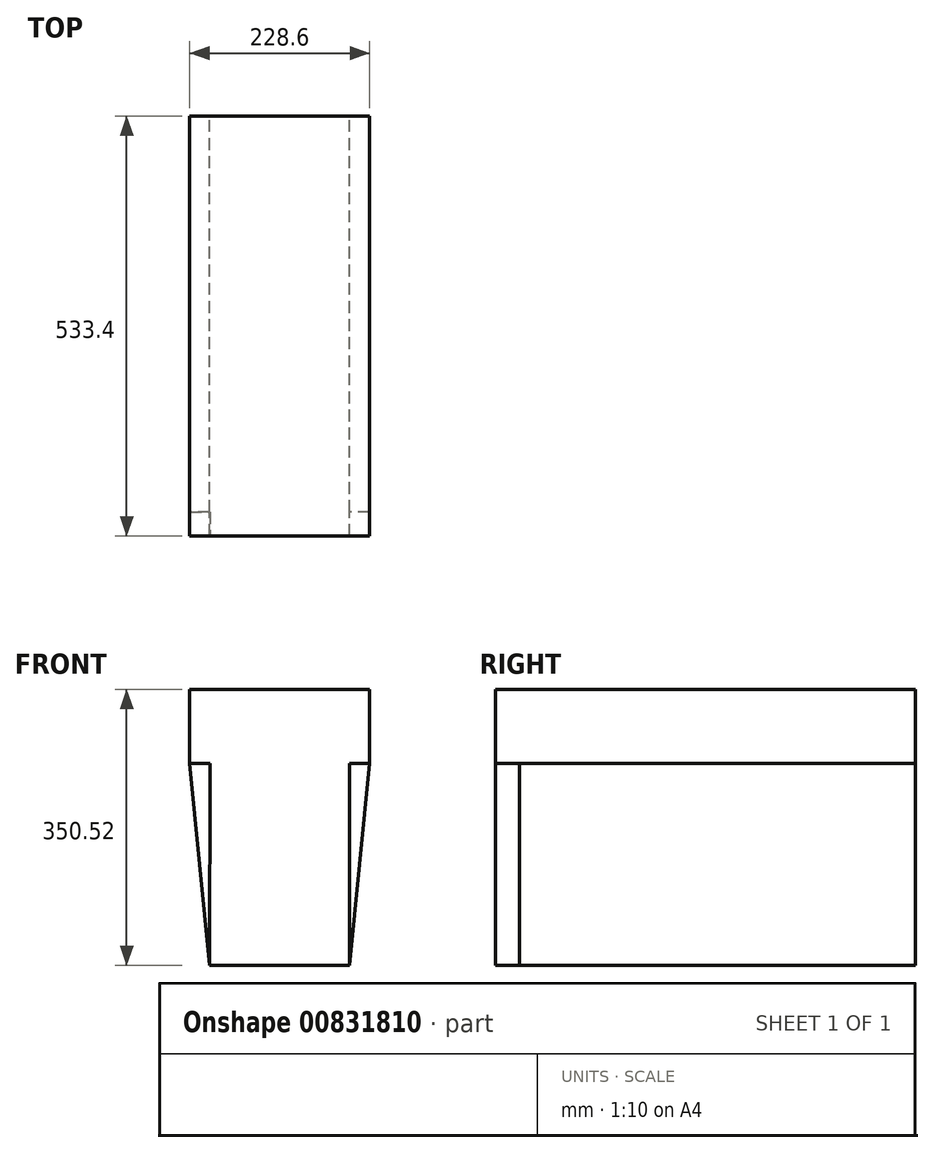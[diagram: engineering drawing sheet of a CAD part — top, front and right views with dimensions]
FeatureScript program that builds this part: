
annotation { "Feature Type Name" : "Feature", "Feature Type Description" : "" }
export const myFeature = defineFeature(function(context is Context, id is Id, definition is map)
    precondition{}
    {
        {
            var Q0;
            Q0=qCreatedBy(makeId("Front.planeOp"),FACE);
            var sketch = newSketch(context, id + "F0", { "sketchPlane" : qUnion([Q0])});
            skLineSegment(sketch, "E0", {"start": v(-248.62, 194.68) * mm, "end": v(-20.02, 194.68) * mm});
            skLineSegment(sketch, "E1", {"start": v(-20.02, 194.68) * mm, "end": v(-20.02, 100.7) * mm});
            skLineSegment(sketch, "E2", {"start": v(-20.02, 100.7) * mm, "end": v(-45.42, -155.84) * mm});
            skLineSegment(sketch, "E3", {"start": v(-45.42, -155.84) * mm, "end": v(-223.22, -155.84) * mm});
            skLineSegment(sketch, "E4", {"start": v(-223.22, -155.84) * mm, "end": v(-248.62, 100.7) * mm});
            skLineSegment(sketch, "E5", {"start": v(-248.62, 100.7) * mm, "end": v(-248.62, 194.68) * mm});
            skLineSegment(sketch, "E6", {"start": v(-248.62, 100.7) * mm, "end": v(-223.22, 100.7) * mm});
            skLineSegment(sketch, "E7", {"start": v(-223.22, 100.7) * mm, "end": v(-224.78, -140.09) * mm});
            skLineSegment(sketch, "E8", {"start": v(-20.02, 100.7) * mm, "end": v(-45.42, 100.7) * mm});
            skLineSegment(sketch, "E9", {"start": v(-45.42, 100.7) * mm, "end": v(-43.86, -140.09) * mm});
            skSolve(sketch);
        }
        {
            var Q0;
            Q0=qSketchRegion(id+"F0",true);
            extrude(context, id + "F1", {"entities" : qUnion([Q0]), "depth" : 533.4 * mm, "offsetDistance" : 25.4 * mm});
        }
        {
            var Q0;
            Q0=makeQuery(id+"F1.opExtrude","CAP_FACE",FACE,{"disambiguationData":[OSD([sQuery(id+"F0.wireOp",EDGE,"E0"),sQuery(id+"F0.wireOp",EDGE,"E1"),sQuery(id+"F0.wireOp",EDGE,"E2"),sQuery(id+"F0.wireOp",EDGE,"E3"),sQuery(id+"F0.wireOp",EDGE,"E4"),sQuery(id+"F0.wireOp",EDGE,"E5")])],"isStart":false});
            var sketch = newSketch(context, id + "F2", { "sketchPlane" : qUnion([Q0])});
            skLineSegment(sketch, "E10", {"start": v(-248.62, 100.7) * mm, "end": v(-223.08, 100.7) * mm});
            skLineSegment(sketch, "E11", {"start": v(-223.22, -155.84) * mm, "end": v(-248.62, 100.7) * mm});
            skLineSegment(sketch, "E12", {"start": v(-15.6, 100.7) * mm, "end": v(-45.42, 100.7) * mm});
            skLineSegment(sketch, "E13", {"start": v(-45.42, 100.7) * mm, "end": v(-45.42, -155.84) * mm});
            skLineSegment(sketch, "E14", {"start": v(-45.42, -155.84) * mm, "end": v(-20.02, 100.7) * mm});
            skLineSegment(sketch, "E15", {"start": v(-223.22, -155.84) * mm, "end": v(-223.08, 100.7) * mm});
            skSolve(sketch);
        }
        {
            var Q0;
            Q0=makeQuery(id+"F2.imprint","IMPRINT",FACE,{"disambiguationData":[TD([[makeQuery(id+"F2.imprint","IMPRINT",EDGE,{"derivedFrom":sQuery(id+"F2.wireOp",EDGE,"E10")}),-1.0]])]});
            var Q1;
            {var subQ2=sQuery(id+"F2.wireOp",EDGE,"E13");Q1=makeQuery(id+"F2.imprint","IMPRINT",FACE,{"disambiguationData":[TD([[makeQuery(id+"F2.imprint","IMPRINT",EDGE,{"derivedFrom":subQ2}),1.0]])]});}
            extrude(context, id + "F3", {"entities" : qUnion([Q0, Q1]), "operationType" : NewBodyOperationType.REMOVE, "oppositeDirection" : true, "depth" : 30.48 * mm, "offsetDistance" : 25.4 * mm});
        }
        {
            var Q0;
            Q0=makeQuery(id+"F0.imprint","IMPRINT",FACE,{"disambiguationData":[TD([[makeQuery(id+"F0.imprint","IMPRINT",EDGE,{"derivedFrom":sQuery(id+"F0.wireOp",EDGE,"E0")}),-1.0]])]});
            var sketch = newSketch(context, id + "F4", { "sketchPlane" : qUnion([Q0])});
            skLineSegment(sketch, "E16", {"start": v(-18.18, 194.82) * mm, "end": v(-246.78, 194.82) * mm});
            skLineSegment(sketch, "E17", {"start": v(-18.18, 194.82) * mm, "end": v(-18.18, 100.84) * mm});
            skLineSegment(sketch, "E18", {"start": v(-18.18, 100.84) * mm, "end": v(-43.58, -153.16) * mm});
            skLineSegment(sketch, "E19", {"start": v(-43.58, -153.16) * mm, "end": v(-221.38, -153.16) * mm});
            skLineSegment(sketch, "E20", {"start": v(-221.38, -153.16) * mm, "end": v(-246.78, 101.86) * mm});
            skLineSegment(sketch, "E21", {"start": v(-246.78, 194.82) * mm, "end": v(-246.78, 101.86) * mm});
            skLineSegment(sketch, "E22", {"start": v(-18.18, 100.84) * mm, "end": v(-45.29, 100.84) * mm});
            skLineSegment(sketch, "E23", {"start": v(-45.29, 100.84) * mm, "end": v(-43.58, -153.16) * mm});
            skLineSegment(sketch, "E24", {"start": v(-222.2, 100.67) * mm, "end": v(-246.78, 101.86) * mm});
            skLineSegment(sketch, "E25", {"start": v(-222.2, 100.67) * mm, "end": v(-221.38, -153.16) * mm});
            skSolve(sketch);
        }
        {
            var Q0;
            {var subQ6=sQuery(id+"F4.wireOp",EDGE,"E18");Q0=makeQuery(id+"F4.imprint","IMPRINT",FACE,{"disambiguationData":[TD([[makeQuery(id+"F4.imprint","IMPRINT",EDGE,{"derivedFrom":subQ6}),-1.0]])]});}
            var Q1;
            {var subQ0=sQuery(id+"F4.wireOp",EDGE,"E20");var subQ1=makeQuery(id+"F0.imprint","IMPRINT",EDGE,{"derivedFrom":sQuery(id+"F0.wireOp",EDGE,"E7")});var subQ2=makeQuery(id+"F4.imprint","INTERSECT",VERTEX,{"derivedFrom":[subQ1,subQ0]});Q1=makeQuery(id+"F4.imprint","IMPRINT",FACE,{"disambiguationData":[TD([[makeQuery(id+"F4.imprint","IMPRINT",EDGE,{"disambiguationData":[TD([[subQ2,-1.0]])],"derivedFrom":subQ0}),-1.0]])]});}
            var Q2;
            {var subQ0=sQuery(id+"F4.wireOp",EDGE,"E24");Q2=makeQuery(id+"F4.imprint","IMPRINT",FACE,{"disambiguationData":[TD([[makeQuery(id+"F4.imprint","IMPRINT",EDGE,{"derivedFrom":subQ0}),1.0]])]});}
            extrude(context, id + "F5", {"entities" : qUnion([Q0, Q1, Q2]), "operationType" : NewBodyOperationType.REMOVE, "oppositeDirection" : true, "depth" : 25.4 * mm, "offsetDistance" : 25.4 * mm});
        }
    });
